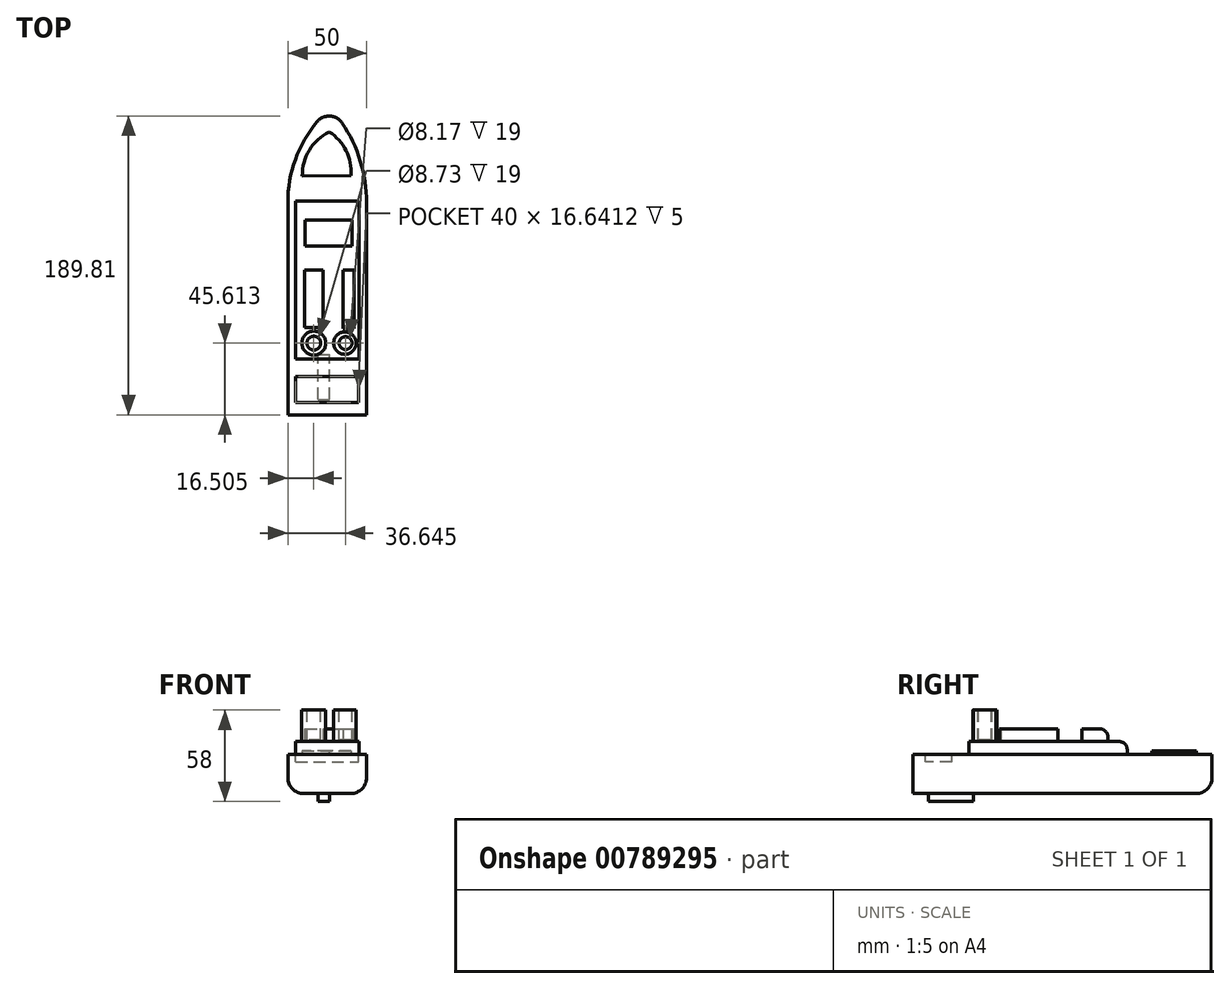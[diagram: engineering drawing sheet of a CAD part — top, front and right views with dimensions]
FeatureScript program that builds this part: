
annotation { "Feature Type Name" : "Feature", "Feature Type Description" : "" }
export const myFeature = defineFeature(function(context is Context, id is Id, definition is map)
    precondition{}
    {
        {
            var Q0;
            Q0=qCreatedBy(makeId("Top.planeOp"),FACE);
            var sketch = newSketch(context, id + "F0", { "sketchPlane" : qUnion([Q0])});
            skLineSegment(sketch, "E0.bottom", {"start": v(-27.08, 42.93) * mm, "end": v(22.92, 42.93) * mm});
            skLineSegment(sketch, "E0.top", {"start": v(-27.08, -92.03) * mm, "end": v(22.92, -92.03) * mm});
            skLineSegment(sketch, "E0.left", {"start": v(-27.08, 42.93) * mm, "end": v(-27.08, -92.03) * mm});
            skLineSegment(sketch, "E0.right", {"start": v(22.92, 42.93) * mm, "end": v(22.92, -92.03) * mm});
            skArc(sketch, "E1", {"start": v(0, 102.93) * mm, "mid": v(-20, 75.85) * mm, "end": v(-27.08, 42.93) * mm});
            skArc(sketch, "E2", {"start": v(22.92, 42.93) * mm, "mid": v(17, 75.05) * mm, "end": v(0, 102.93) * mm});
            skSolve(sketch);
        }
        {
            var Q0;
            Q0=makeQuery(id+"F0.imprint","IMPRINT",FACE,{"disambiguationData":[TD([[makeQuery(id+"F0.imprint","IMPRINT",EDGE,{"derivedFrom":sQuery(id+"F0.wireOp",EDGE,"E0.bottom")}),1.0]])]});
            extrude(context, id + "F1", {"entities" : qUnion([Q0]), "depth" : 25 * mm, "offsetDistance" : 25 * mm});
        }
        {
            var Q0;
            Q0 = qSketchRegion(id + "F0", true);
            extrude(context, id + "F2", {"entities" : qUnion([Q0]), "operationType" : NewBodyOperationType.ADD, "depth" : 25 * mm, "offsetDistance" : 25 * mm});
        }
        {
            var Q0;
            {var subQ0=sQuery(id+"F0.wireOp",EDGE,"E2");var subQ1=sQuery(id+"F0.wireOp",EDGE,"E1");Q0=makeQuery(id+"F2.boolean.opBoolean","MERGE",FACE,{"derivedFrom":[makeQuery(id+"F1.opExtrude","CAP_FACE",FACE,{"disambiguationData":[OSD([sQuery(id+"F0.wireOp",EDGE,"E0.bottom"),subQ1,subQ0])],"isStart":false}),makeQuery(id+"F2.opExtrude","CAP_FACE",FACE,{"disambiguationData":[OSD([sQuery(id+"F0.wireOp",EDGE,"E0.top"),sQuery(id+"F0.wireOp",EDGE,"E0.left"),sQuery(id+"F0.wireOp",EDGE,"E0.right"),subQ1,subQ0])],"isStart":false})]});}
            var sketch = newSketch(context, id + "F3", { "sketchPlane" : qUnion([Q0])});
            skLineSegment(sketch, "E3.bottom", {"start": v(-22.28, 43.93) * mm, "end": v(18.23, 43.93) * mm});
            skLineSegment(sketch, "E3.top", {"start": v(-22.28, -56.6) * mm, "end": v(18.23, -56.6) * mm});
            skLineSegment(sketch, "E3.left", {"start": v(-22.28, 43.93) * mm, "end": v(-22.28, -56.6) * mm});
            skLineSegment(sketch, "E3.right", {"start": v(18.23, 43.93) * mm, "end": v(18.23, -56.6) * mm});
            skSolve(sketch);
        }
        {
            var Q0;
            Q0=makeQuery(id+"F3.imprint","IMPRINT",FACE,{"disambiguationData":[TD([[makeQuery(id+"F3.imprint","IMPRINT",EDGE,{"derivedFrom":sQuery(id+"F3.wireOp",EDGE,"E3.bottom")}),-1.0]])]});
            extrude(context, id + "F4", {"entities" : qUnion([Q0]), "operationType" : NewBodyOperationType.ADD, "depth" : 8 * mm, "offsetDistance" : 25 * mm});
        }
        {
            var Q0;
            Q0=makeQuery(id+"F2.opExtrude","CAP_EDGE",EDGE,{"disambiguationData":[OSD([sQuery(id+"F0.wireOp",EDGE,"E0.right")])],"isStart":true});
            fillet(context, id + "F5", {"entities" : qUnion([Q0]), "radius" : 10 * mm, "tangentPropagation" : true, "allowEdgeOverflow" : false});
        }
        {
            var Q0;
            Q0=makeQuery(id+"F2.opExtrude","CAP_EDGE",EDGE,{"disambiguationData":[OSD([sQuery(id+"F0.wireOp",EDGE,"E0.left")])],"isStart":true});
            fillet(context, id + "F6", {"entities" : qUnion([Q0]), "radius" : 10 * mm, "tangentPropagation" : true, "allowEdgeOverflow" : false});
        }
        {
            var Q0;
            Q0=makeQuery(id+"F4.opExtrude","CAP_FACE",FACE,{"disambiguationData":[OSD([sQuery(id+"F3.wireOp",EDGE,"E3.bottom"),sQuery(id+"F3.wireOp",EDGE,"E3.top"),sQuery(id+"F3.wireOp",EDGE,"E3.left"),sQuery(id+"F3.wireOp",EDGE,"E3.right")])],"isStart":false});
            var sketch = newSketch(context, id + "F7", { "sketchPlane" : qUnion([Q0])});
            skLineSegment(sketch, "E4.bottom", {"start": v(-16.06, 31.73) * mm, "end": v(13.77, 31.73) * mm});
            skLineSegment(sketch, "E4.top", {"start": v(-16.06, 15.24) * mm, "end": v(13.77, 15.24) * mm});
            skLineSegment(sketch, "E4.left", {"start": v(-16.06, 31.73) * mm, "end": v(-16.06, 15.24) * mm});
            skLineSegment(sketch, "E4.right", {"start": v(13.77, 31.73) * mm, "end": v(13.77, 15.24) * mm});
            skSolve(sketch);
        }
        {
            var Q0;
            Q0=makeQuery(id+"F7.imprint","IMPRINT",FACE,{"disambiguationData":[TD([[makeQuery(id+"F7.imprint","IMPRINT",EDGE,{"derivedFrom":sQuery(id+"F7.wireOp",EDGE,"E4.bottom")}),-1.0]])]});
            extrude(context, id + "F8", {"entities" : qUnion([Q0]), "operationType" : NewBodyOperationType.ADD, "depth" : 8 * mm, "offsetDistance" : 25 * mm});
        }
        {
            var Q0;
            Q0=makeQuery(id+"F4.opExtrude","CAP_FACE",FACE,{"disambiguationData":[OSD([sQuery(id+"F3.wireOp",EDGE,"E3.bottom"),sQuery(id+"F3.wireOp",EDGE,"E3.top"),sQuery(id+"F3.wireOp",EDGE,"E3.left"),sQuery(id+"F3.wireOp",EDGE,"E3.right")])],"isStart":false});
            var sketch = newSketch(context, id + "F9", { "sketchPlane" : qUnion([Q0])});
            skLineSegment(sketch, "E5.bottom", {"start": v(-16.3, 0) * mm, "end": v(-4.84, 0) * mm});
            skLineSegment(sketch, "E5.top", {"start": v(-16.3, -36.38) * mm, "end": v(-4.84, -36.38) * mm});
            skLineSegment(sketch, "E5.left", {"start": v(-16.3, 0) * mm, "end": v(-16.3, -36.38) * mm});
            skLineSegment(sketch, "E5.right", {"start": v(-4.84, 0) * mm, "end": v(-4.84, -36.38) * mm});
            skLineSegment(sketch, "E6.bottom", {"start": v(8.07, 0) * mm, "end": v(14.88, 0) * mm});
            skLineSegment(sketch, "E6.top", {"start": v(8.07, -37.1) * mm, "end": v(14.88, -37.1) * mm});
            skLineSegment(sketch, "E6.left", {"start": v(8.07, 0) * mm, "end": v(8.07, -37.1) * mm});
            skLineSegment(sketch, "E6.right", {"start": v(14.88, 0) * mm, "end": v(14.88, -37.1) * mm});
            skSolve(sketch);
        }
        {
            var Q0;
            Q0=makeQuery(id+"F9.imprint","IMPRINT",FACE,{"disambiguationData":[TD([[makeQuery(id+"F9.imprint","IMPRINT",EDGE,{"derivedFrom":sQuery(id+"F9.wireOp",EDGE,"E5.bottom")}),-1.0]])]});
            var Q1;
            Q1=makeQuery(id+"F9.imprint","IMPRINT",FACE,{"disambiguationData":[TD([[makeQuery(id+"F9.imprint","IMPRINT",EDGE,{"derivedFrom":sQuery(id+"F9.wireOp",EDGE,"E6.bottom")}),-1.0]])]});
            extrude(context, id + "F10", {"entities" : qUnion([Q0, Q1]), "operationType" : NewBodyOperationType.ADD, "depth" : 8 * mm, "offsetDistance" : 25 * mm});
        }
        {
            var Q0;
            Q0=makeQuery(id+"F8.opExtrude","CAP_EDGE",EDGE,{"disambiguationData":[OSD([sQuery(id+"F7.wireOp",EDGE,"E4.bottom")])],"isStart":false});
            var Q1;
            Q1=makeQuery(id+"F4.opExtrude","CAP_EDGE",EDGE,{"disambiguationData":[OSD([sQuery(id+"F3.wireOp",EDGE,"E3.bottom")])],"isStart":false});
            fillet(context, id + "F11", {"entities" : qUnion([Q0, Q1]), "radius" : 5 * mm, "tangentPropagation" : true, "allowEdgeOverflow" : false});
        }
        {
            var Q0;
            {var subQ0=sQuery(id+"F0.wireOp",EDGE,"E2");var subQ1=sQuery(id+"F0.wireOp",EDGE,"E1");Q0=makeQuery(id+"F2.boolean.opBoolean","MERGE",FACE,{"derivedFrom":[makeQuery(id+"F1.opExtrude","CAP_FACE",FACE,{"disambiguationData":[OSD([sQuery(id+"F0.wireOp",EDGE,"E0.bottom"),subQ1,subQ0])],"isStart":false}),makeQuery(id+"F2.opExtrude","CAP_FACE",FACE,{"disambiguationData":[OSD([sQuery(id+"F0.wireOp",EDGE,"E0.top"),sQuery(id+"F0.wireOp",EDGE,"E0.left"),sQuery(id+"F0.wireOp",EDGE,"E0.right"),subQ1,subQ0])],"isStart":false})]});}
            var sketch = newSketch(context, id + "F12", { "sketchPlane" : qUnion([Q0])});
            skLineSegment(sketch, "E7.bottom", {"start": v(-22.08, -67.49) * mm, "end": v(17.92, -67.49) * mm});
            skLineSegment(sketch, "E7.top", {"start": v(-22.08, -84.13) * mm, "end": v(17.92, -84.13) * mm});
            skLineSegment(sketch, "E7.left", {"start": v(-22.08, -67.49) * mm, "end": v(-22.08, -84.13) * mm});
            skLineSegment(sketch, "E7.right", {"start": v(17.92, -67.49) * mm, "end": v(17.92, -84.13) * mm});
            skSolve(sketch);
        }
        {
            var Q0;
            Q0=makeQuery(id+"F12.imprint","IMPRINT",FACE,{"disambiguationData":[TD([[makeQuery(id+"F12.imprint","IMPRINT",EDGE,{"derivedFrom":sQuery(id+"F12.wireOp",EDGE,"E7.bottom")}),-1.0]])]});
            extrude(context, id + "F13", {"entities" : qUnion([Q0]), "operationType" : NewBodyOperationType.REMOVE, "oppositeDirection" : true, "depth" : 5 * mm, "offsetDistance" : 25 * mm});
        }
        {
            var Q0;
            Q0=makeQuery(id+"F4.opExtrude","CAP_FACE",FACE,{"disambiguationData":[OSD([sQuery(id+"F3.wireOp",EDGE,"E3.bottom"),sQuery(id+"F3.wireOp",EDGE,"E3.top"),sQuery(id+"F3.wireOp",EDGE,"E3.left"),sQuery(id+"F3.wireOp",EDGE,"E3.right")])],"isStart":false});
            var sketch = newSketch(context, id + "F14", { "sketchPlane" : qUnion([Q0])});
            skCircle(sketch, "E8", {"center": v(-10.57, -46.42) * mm, "radius": 7.62 * mm});
            skCircle(sketch, "E9", {"center": v(9.14, -46.42) * mm, "radius": 7.14 * mm});
            skSolve(sketch);
        }
        {
            var Q0;
            Q0=makeQuery(id+"F14.imprint","IMPRINT",FACE,{"disambiguationData":[TD([[makeQuery(id+"F14.imprint","IMPRINT",EDGE,{"derivedFrom":sQuery(id+"F14.wireOp",EDGE,"E8")}),1.0]])]});
            var Q1;
            Q1=makeQuery(id+"F14.imprint","IMPRINT",FACE,{"disambiguationData":[TD([[makeQuery(id+"F14.imprint","IMPRINT",EDGE,{"derivedFrom":sQuery(id+"F14.wireOp",EDGE,"E9")}),1.0]])]});
            extrude(context, id + "F15", {"entities" : qUnion([Q0, Q1]), "operationType" : NewBodyOperationType.ADD, "depth" : 20 * mm, "offsetDistance" : 25 * mm});
        }
        {
            var Q0;
            Q0=makeQuery(id+"F15.opExtrude","CAP_FACE",FACE,{"disambiguationData":[OSD([sQuery(id+"F14.wireOp",EDGE,"E8")])],"isStart":false});
            var sketch = newSketch(context, id + "F16", { "sketchPlane" : qUnion([Q0])});
            skCircle(sketch, "E10", {"center": v(-10.57, -46.42) * mm, "radius": 4.37 * mm});
            skCircle(sketch, "E11", {"center": v(9.56, -46.42) * mm, "radius": 4.09 * mm});
            skSolve(sketch);
        }
        {
            var Q0;
            Q0=makeQuery(id+"F16.imprint","IMPRINT",FACE,{"disambiguationData":[TD([[makeQuery(id+"F16.imprint","IMPRINT",EDGE,{"derivedFrom":sQuery(id+"F16.wireOp",EDGE,"E10")}),1.0]])]});
            var Q1;
            Q1=makeQuery(id+"F16.imprint","IMPRINT",FACE,{"disambiguationData":[TD([[makeQuery(id+"F16.imprint","IMPRINT",EDGE,{"derivedFrom":sQuery(id+"F16.wireOp",EDGE,"E11")}),1.0]])]});
            extrude(context, id + "F17", {"entities" : qUnion([Q0, Q1]), "operationType" : NewBodyOperationType.REMOVE, "oppositeDirection" : true, "depth" : 19 * mm, "offsetDistance" : 25 * mm});
        }
        {
            var Q0;
            {var subQ0=sQuery(id+"F0.wireOp",EDGE,"E2");var subQ1=sQuery(id+"F0.wireOp",EDGE,"E1");Q0=makeQuery(id+"F2.boolean.opBoolean","MERGE",FACE,{"derivedFrom":[makeQuery(id+"F1.opExtrude","CAP_FACE",FACE,{"disambiguationData":[OSD([sQuery(id+"F0.wireOp",EDGE,"E0.bottom"),subQ1,subQ0])],"isStart":true}),makeQuery(id+"F2.opExtrude","CAP_FACE",FACE,{"disambiguationData":[OSD([sQuery(id+"F0.wireOp",EDGE,"E0.top"),sQuery(id+"F0.wireOp",EDGE,"E0.left"),sQuery(id+"F0.wireOp",EDGE,"E0.right"),subQ1,subQ0])],"isStart":true})]});}
            var sketch = newSketch(context, id + "F18", { "sketchPlane" : qUnion([Q0])});
            skLineSegment(sketch, "E12.bottom", {"start": v(-8, 82.26) * mm, "end": v(-0.47, 82.26) * mm});
            skLineSegment(sketch, "E12.top", {"start": v(-8, 53.59) * mm, "end": v(-0.47, 53.59) * mm});
            skLineSegment(sketch, "E12.left", {"start": v(-8, 82.26) * mm, "end": v(-8, 53.59) * mm});
            skLineSegment(sketch, "E12.right", {"start": v(-0.47, 82.26) * mm, "end": v(-0.47, 53.59) * mm});
            skSolve(sketch);
        }
        {
            var Q0;
            Q0=makeQuery(id+"F18.imprint","IMPRINT",FACE,{"disambiguationData":[TD([[makeQuery(id+"F18.imprint","IMPRINT",EDGE,{"derivedFrom":sQuery(id+"F18.wireOp",EDGE,"E12.bottom")}),-1.0]])]});
            extrude(context, id + "F19", {"entities" : qUnion([Q0]), "operationType" : NewBodyOperationType.ADD, "depth" : 5 * mm, "offsetDistance" : 25 * mm});
        }
        {
            var Q0;
            {var subQ0=sQuery(id+"F0.wireOp",EDGE,"E2");var subQ1=sQuery(id+"F0.wireOp",EDGE,"E1");Q0=makeQuery(id+"F2.boolean.opBoolean","MERGE",FACE,{"derivedFrom":[makeQuery(id+"F1.opExtrude","CAP_FACE",FACE,{"disambiguationData":[OSD([sQuery(id+"F0.wireOp",EDGE,"E0.bottom"),subQ1,subQ0])],"isStart":false}),makeQuery(id+"F2.opExtrude","CAP_FACE",FACE,{"disambiguationData":[OSD([sQuery(id+"F0.wireOp",EDGE,"E0.top"),sQuery(id+"F0.wireOp",EDGE,"E0.left"),sQuery(id+"F0.wireOp",EDGE,"E0.right"),subQ1,subQ0])],"isStart":false})]});}
            var sketch = newSketch(context, id + "F20", { "sketchPlane" : qUnion([Q0])});
            skArc(sketch, "E13", {"start": v(-0.83, 87.78) * mm, "mid": v(-13.4, 76.16) * mm, "end": v(-17.9, 59.66) * mm});
            skArc(sketch, "E14", {"start": v(13.15, 60.05) * mm, "mid": v(9.9, 75.8) * mm, "end": v(-0.83, 87.78) * mm});
            skLineSegment(sketch, "E15", {"start": v(-17.9, 59.66) * mm, "end": v(13.15, 60.05) * mm});
            skSolve(sketch);
        }
        {
            var Q0;
            Q0=makeQuery(id+"F20.imprint","IMPRINT",FACE,{"disambiguationData":[TD([[makeQuery(id+"F20.imprint","IMPRINT",EDGE,{"derivedFrom":sQuery(id+"F20.wireOp",EDGE,"E13")}),1.0]])]});
            extrude(context, id + "F21", {"entities" : qUnion([Q0]), "operationType" : NewBodyOperationType.ADD, "depth" : 2 * mm, "offsetDistance" : 25 * mm});
        }
    });
